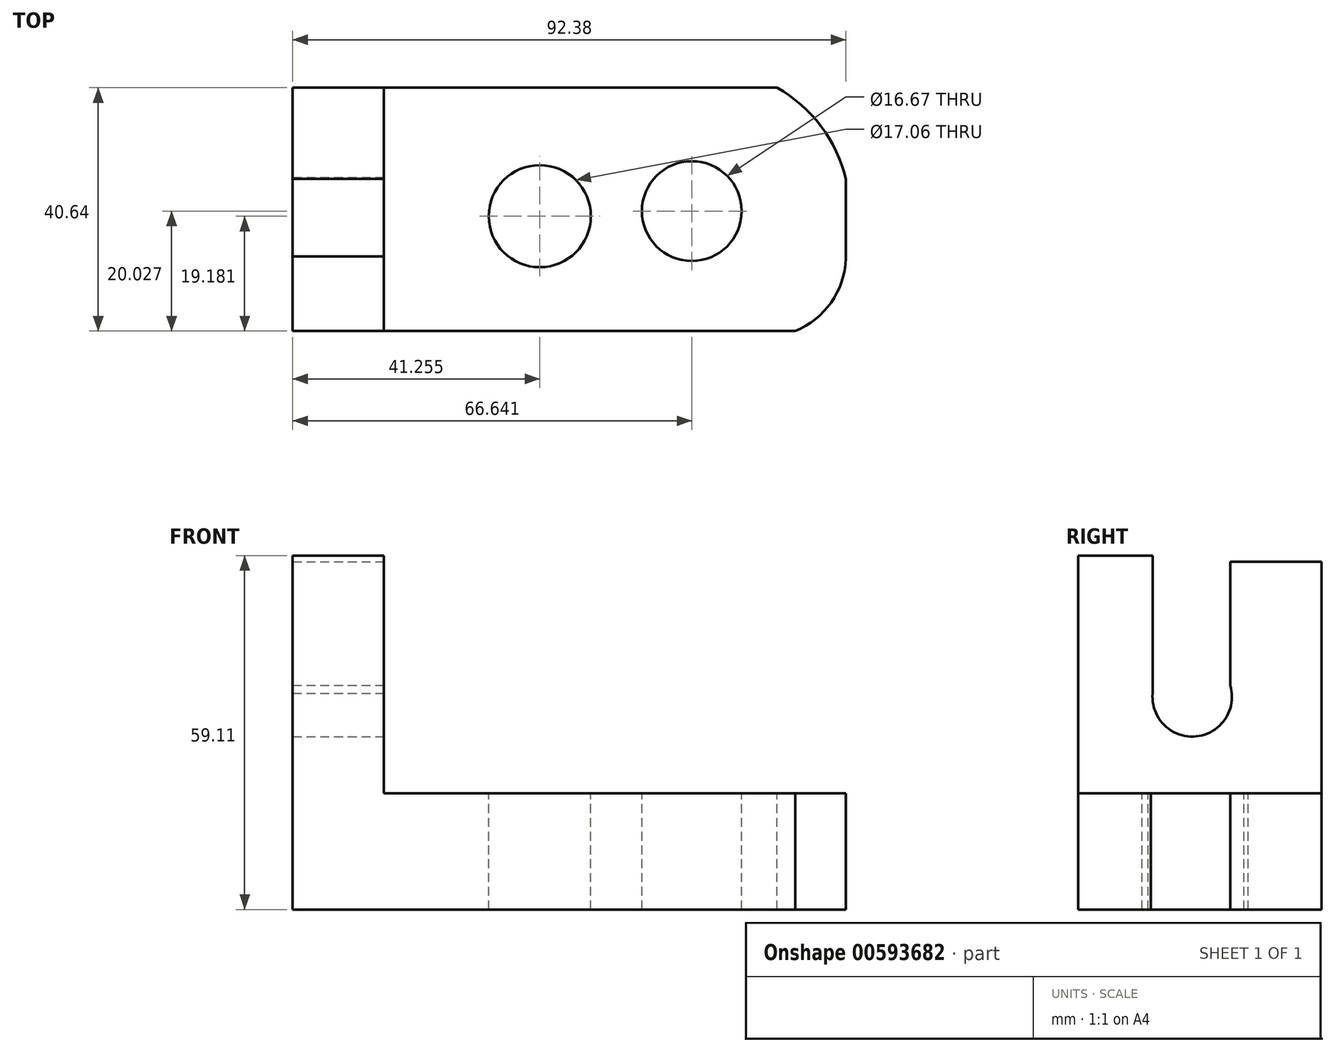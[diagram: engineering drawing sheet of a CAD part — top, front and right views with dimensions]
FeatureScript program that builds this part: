
annotation { "Feature Type Name" : "Feature", "Feature Type Description" : "" }
export const myFeature = defineFeature(function(context is Context, id is Id, definition is map)
    precondition{}
    {
        {
            var Q0;
            Q0=qCreatedBy(makeId("Front.planeOp"),FACE);
            var sketch = newSketch(context, id + "F0", { "sketchPlane" : qUnion([Q0])});
            skLineSegment(sketch, "E0", {"start": v(-73.65, 0) * mm, "end": v(-73.65, 52.25) * mm});
            skLineSegment(sketch, "E1", {"start": v(-73.96, 52.25) * mm, "end": v(-58.46, 52.25) * mm});
            skLineSegment(sketch, "E2", {"start": v(-58.46, 52.25) * mm, "end": v(-58.46, 19.38) * mm});
            skLineSegment(sketch, "E3", {"start": v(-58.46, 19.38) * mm, "end": v(-6.67, 19.38) * mm});
            skLineSegment(sketch, "E4", {"start": v(-6.67, 19.38) * mm, "end": v(-6.67, 0) * mm});
            skLineSegment(sketch, "E5", {"start": v(-6.67, 0) * mm, "end": v(-73.65, 0) * mm});
            skSolve(sketch);
        }
        {
            var Q0;
            {var subQ2=sQuery(id+"F0.wireOp",EDGE,"E0");Q0=makeQuery(id+"F0.imprint","IMPRINT",FACE,{"disambiguationData":[TD([[makeQuery(id+"F0.imprint","IMPRINT",EDGE,{"derivedFrom":subQ2}),-1.0]])]});}
            extrude(context, id + "F1", {"entities" : qUnion([Q0]), "depth" : 25.4 * mm, "offsetDistance" : 25.4 * mm});
        }
        {
            var Q0;
            Q0=makeQuery(id+"F1.opExtrude","CAP_FACE",FACE,{"disambiguationData":[OSD([sQuery(id+"F0.wireOp",EDGE,"E0"),sQuery(id+"F0.wireOp",EDGE,"E1"),sQuery(id+"F0.wireOp",EDGE,"E2"),sQuery(id+"F0.wireOp",EDGE,"E3"),sQuery(id+"F0.wireOp",EDGE,"E4"),sQuery(id+"F0.wireOp",EDGE,"E5")])],"isStart":true});
            extrude(context, id + "F2", {"entities" : qUnion([Q0]), "operationType" : NewBodyOperationType.ADD, "depth" : 15.24 * mm, "offsetDistance" : 25.4 * mm});
        }
        {
            var Q0;
            {var subQ0=sQuery(id+"F0.wireOp",EDGE,"E4");Q0=makeQuery(id+"F2.boolean.opBoolean","MERGE",FACE,{"derivedFrom":[makeQuery(id+"F1.opExtrude","SWEPT_FACE",FACE,{"disambiguationData":[OSD([subQ0])]}),makeQuery(id+"F2.opExtrude","SWEPT_FACE",FACE,{"disambiguationData":[OSD([subQ0])]})]});}
            extrude(context, id + "F3", {"entities" : qUnion([Q0]), "operationType" : NewBodyOperationType.ADD, "depth" : 25.4 * mm, "offsetDistance" : 25.4 * mm});
        }
        {
            var Q0;
            {var subQ0=sQuery(id+"F0.wireOp",EDGE,"E1");Q0=makeQuery(id+"F2.boolean.opBoolean","MERGE",FACE,{"derivedFrom":[makeQuery(id+"F1.opExtrude","SWEPT_FACE",FACE,{"disambiguationData":[OSD([subQ0])]}),makeQuery(id+"F2.opExtrude","SWEPT_FACE",FACE,{"disambiguationData":[OSD([subQ0])]})]});}
            extrude(context, id + "F4", {"entities" : qUnion([Q0]), "operationType" : NewBodyOperationType.ADD, "depth" : 10.4 * mm, "offsetDistance" : 25.4 * mm});
        }
        {
            var Q0;
            {var subQ0=sQuery(id+"F0.wireOp",EDGE,"E3");Q0=makeQuery(id+"F3.boolean.opBoolean","MERGE",FACE,{"derivedFrom":[makeQuery(id+"F2.boolean.opBoolean","MERGE",FACE,{"derivedFrom":[makeQuery(id+"F1.opExtrude","SWEPT_FACE",FACE,{"disambiguationData":[OSD([subQ0])]}),makeQuery(id+"F2.opExtrude","SWEPT_FACE",FACE,{"disambiguationData":[OSD([subQ0])]})]}),makeQuery(id+"F3.opExtrude","SWEPT_FACE",FACE,{"disambiguationData":[OSD([subQ0,sQuery(id+"F0.wireOp",EDGE,"E4")])]})]});}
            var sketch = newSketch(context, id + "F5", { "sketchPlane" : qUnion([Q0])});
            skCircle(sketch, "E6", {"center": v(-32.4, -6.22) * mm, "radius": 8.53 * mm});
            skCircle(sketch, "E7", {"center": v(-7, -5.37) * mm, "radius": 8.33 * mm});
            skSolve(sketch);
        }
        {
            var Q0;
            Q0=makeQuery(id+"F5.imprint","IMPRINT",FACE,{"disambiguationData":[TD([[makeQuery(id+"F5.imprint","IMPRINT",EDGE,{"derivedFrom":sQuery(id+"F5.wireOp",EDGE,"E6")}),1.0]])]});
            var Q1;
            Q1=makeQuery(id+"F5.imprint","IMPRINT",FACE,{"disambiguationData":[TD([[makeQuery(id+"F5.imprint","IMPRINT",EDGE,{"derivedFrom":sQuery(id+"F5.wireOp",EDGE,"E7")}),1.0]])]});
            extrude(context, id + "F6", {"entities" : qUnion([Q0, Q1]), "operationType" : NewBodyOperationType.REMOVE, "oppositeDirection" : true, "depth" : 25.4 * mm, "offsetDistance" : 25.4 * mm});
        }
        {
            var Q0;
            {var subQ0=sQuery(id+"F0.wireOp",EDGE,"E2");Q0=makeQuery(id+"F4.boolean.opBoolean","MERGE",FACE,{"derivedFrom":[makeQuery(id+"F2.boolean.opBoolean","MERGE",FACE,{"derivedFrom":[makeQuery(id+"F1.opExtrude","SWEPT_FACE",FACE,{"disambiguationData":[OSD([subQ0])]}),makeQuery(id+"F2.opExtrude","SWEPT_FACE",FACE,{"disambiguationData":[OSD([subQ0])]})]}),makeQuery(id+"F4.opExtrude","SWEPT_FACE",FACE,{"disambiguationData":[OSD([sQuery(id+"F0.wireOp",EDGE,"E1"),subQ0])]})]});}
            var sketch = newSketch(context, id + "F7", { "sketchPlane" : qUnion([Q0])});
            skLineSegment(sketch, "E8", {"start": v(-12.56, 62.67) * mm, "end": v(-12.56, 38.6) * mm});
            skLineSegment(sketch, "E9", {"start": v(0, 62.67) * mm, "end": v(0, 38.6) * mm});
            skPoint(sketch, "E9.startSnap0", {"position": v(-5.08, 62.67) * mm});
            skCircle(sketch, "E10", {"center": v(-6.36, 35.5) * mm, "radius": 6.64 * mm});
            skSolve(sketch);
        }
        {
            var Q0;
            Q0=makeQuery(id+"F7.imprint","IMPRINT",FACE,{"disambiguationData":[TD([[makeQuery(id+"F7.imprint","IMPRINT",EDGE,{"derivedFrom":sQuery(id+"F7.wireOp",EDGE,"E10")}),1.0]])]});
            extrude(context, id + "F8", {"entities" : qUnion([Q0]), "operationType" : NewBodyOperationType.REMOVE, "oppositeDirection" : true, "depth" : 25.4 * mm, "offsetDistance" : 25.4 * mm});
        }
        {
            var Q0;
            {var subQ0=sQuery(id+"F0.wireOp",EDGE,"E2");Q0=makeQuery(id+"F4.boolean.opBoolean","MERGE",FACE,{"derivedFrom":[makeQuery(id+"F2.boolean.opBoolean","MERGE",FACE,{"derivedFrom":[makeQuery(id+"F1.opExtrude","SWEPT_FACE",FACE,{"disambiguationData":[OSD([subQ0])]}),makeQuery(id+"F2.opExtrude","SWEPT_FACE",FACE,{"disambiguationData":[OSD([subQ0])]})]}),makeQuery(id+"F4.opExtrude","SWEPT_FACE",FACE,{"disambiguationData":[OSD([sQuery(id+"F0.wireOp",EDGE,"E1"),subQ0])]})]});}
            var sketch = newSketch(context, id + "F9", { "sketchPlane" : qUnion([Q0])});
            skLineSegment(sketch, "E11", {"start": v(-12.97, 34.9) * mm, "end": v(-12.97, 62.67) * mm});
            skLineSegment(sketch, "E12", {"start": v(-12.97, 62.67) * mm, "end": v(0, 62.67) * mm});
            skLineSegment(sketch, "E13", {"start": v(0, 62.67) * mm, "end": v(0, 37.41) * mm});
            skSolve(sketch);
        }
        {
            var Q0;
            {var subQ0=sQuery(id+"F9.wireOp",EDGE,"E12");Q0=makeQuery(id+"F9.imprint","IMPRINT",FACE,{"disambiguationData":[TD([[makeQuery(id+"F9.imprint","IMPRINT",EDGE,{"derivedFrom":subQ0}),-1.0]])]});}
            extrude(context, id + "F10", {"entities" : qUnion([Q0]), "operationType" : NewBodyOperationType.REMOVE, "oppositeDirection" : true, "depth" : 63.25 * mm, "offsetDistance" : 25.4 * mm});
        }
        {
            var Q0;
            {var subQ0=sQuery(id+"F0.wireOp",EDGE,"E3");Q0=makeQuery(id+"F3.boolean.opBoolean","MERGE",FACE,{"derivedFrom":[makeQuery(id+"F2.boolean.opBoolean","MERGE",FACE,{"derivedFrom":[makeQuery(id+"F1.opExtrude","SWEPT_FACE",FACE,{"disambiguationData":[OSD([subQ0])]}),makeQuery(id+"F2.opExtrude","SWEPT_FACE",FACE,{"disambiguationData":[OSD([subQ0])]})]}),makeQuery(id+"F3.opExtrude","SWEPT_FACE",FACE,{"disambiguationData":[OSD([subQ0,sQuery(id+"F0.wireOp",EDGE,"E4")])]})]});}
            var sketch = newSketch(context, id + "F11", { "sketchPlane" : qUnion([Q0])});
            skArc(sketch, "E14", {"start": v(0, -25.4) * mm, "mid": v(12.52, -24.21) * mm, "end": v(18.73, -13.29) * mm});
            skSolve(sketch);
        }
        {
            var Q0;
            {var subQ0=sQuery(id+"F11.wireOp",EDGE,"E14");var subQ1=sQuery(id+"F0.wireOp",EDGE,"E4");var subQ2=sQuery(id+"F0.wireOp",EDGE,"E3");var subQ3=makeQuery(id+"F3.opExtrude","CAP_EDGE",EDGE,{"disambiguationData":[OSD([subQ2,subQ1])],"isStart":false});var subQ4=makeQuery(id+"F11.imprint","INTERSECT",VERTEX,{"derivedFrom":[subQ3,subQ0]});Q0=makeQuery(id+"F11.imprint","IMPRINT",FACE,{"disambiguationData":[TD([[makeQuery(id+"F11.imprint","IMPRINT",EDGE,{"disambiguationData":[TD([[subQ4,1.0]])],"derivedFrom":subQ0}),-1.0]])]});}
            extrude(context, id + "F12", {"entities" : qUnion([Q0]), "operationType" : NewBodyOperationType.ADD, "depth" : 25.4 * mm, "offsetDistance" : 25.4 * mm});
        }
        {
            var Q0;
            {var subQ0=sQuery(id+"F0.wireOp",EDGE,"E3");Q0=makeQuery(id+"F3.boolean.opBoolean","MERGE",FACE,{"derivedFrom":[makeQuery(id+"F2.boolean.opBoolean","MERGE",FACE,{"derivedFrom":[makeQuery(id+"F1.opExtrude","SWEPT_FACE",FACE,{"disambiguationData":[OSD([subQ0])]}),makeQuery(id+"F2.opExtrude","SWEPT_FACE",FACE,{"disambiguationData":[OSD([subQ0])]})]}),makeQuery(id+"F3.opExtrude","SWEPT_FACE",FACE,{"disambiguationData":[OSD([subQ0,sQuery(id+"F0.wireOp",EDGE,"E4")])]})]});}
            var sketch = newSketch(context, id + "F13", { "sketchPlane" : qUnion([Q0])});
            skArc(sketch, "E15", {"start": v(18.73, 0) * mm, "mid": v(14.55, 8.82) * mm, "end": v(7.2, 15.24) * mm});
            skSolve(sketch);
        }
        {
            var Q0;
            {var subQ0=sQuery(id+"F13.wireOp",EDGE,"E15");Q0=makeQuery(id+"F13.imprint","IMPRINT",FACE,{"disambiguationData":[TD([[makeQuery(id+"F13.imprint","IMPRINT",EDGE,{"derivedFrom":subQ0}),-1.0]])]});}
            extrude(context, id + "F14", {"entities" : qUnion([Q0]), "operationType" : NewBodyOperationType.REMOVE, "oppositeDirection" : true, "depth" : 25.4 * mm, "offsetDistance" : 25.4 * mm});
        }
        {
            var Q0;
            Q0=makeQuery(id+"F12.opExtrude","CAP_FACE",FACE,{"disambiguationData":[OSD([sQuery(id+"F0.wireOp",EDGE,"E3"),sQuery(id+"F0.wireOp",EDGE,"E4"),sQuery(id+"F11.wireOp",EDGE,"E14")])],"isStart":false});
            extrude(context, id + "F15", {"entities" : qUnion([Q0]), "operationType" : NewBodyOperationType.REMOVE, "oppositeDirection" : true, "depth" : 72.64 * mm, "offsetDistance" : 25.4 * mm});
        }
        {
            var Q0;
            {var subQ3=sQuery(id+"F0.wireOp",EDGE,"E1");Q0=makeQuery(id+"F10.boolean.opBoolean","SPLIT",FACE,{"disambiguationData":[TD([makeQuery(id+"F10.opExtrude","SWEPT_FACE",FACE,{"disambiguationData":[OSD([sQuery(id+"F9.wireOp",EDGE,"E11")])]})])],"derivedFrom":makeQuery(id+"F4.opExtrude","CAP_FACE",FACE,{"disambiguationData":[OSD([subQ3])],"isStart":false})});}
            extrude(context, id + "F16", {"entities" : qUnion([Q0]), "operationType" : NewBodyOperationType.REMOVE, "oppositeDirection" : true, "depth" : 3.56 * mm, "offsetDistance" : 25.4 * mm});
        }
        {
            var Q0;
            {var subQ3=sQuery(id+"F0.wireOp",EDGE,"E1");Q0=makeQuery(id+"F10.boolean.opBoolean","SPLIT",FACE,{"disambiguationData":[TD([makeQuery(id+"F10.opExtrude","SWEPT_FACE",FACE,{"disambiguationData":[OSD([sQuery(id+"F9.wireOp",EDGE,"E13")])]})])],"derivedFrom":makeQuery(id+"F4.opExtrude","CAP_FACE",FACE,{"disambiguationData":[OSD([subQ3])],"isStart":false})});}
            extrude(context, id + "F17", {"entities" : qUnion([Q0]), "operationType" : NewBodyOperationType.REMOVE, "oppositeDirection" : true, "depth" : 4.57 * mm, "offsetDistance" : 25.4 * mm});
        }
    });
